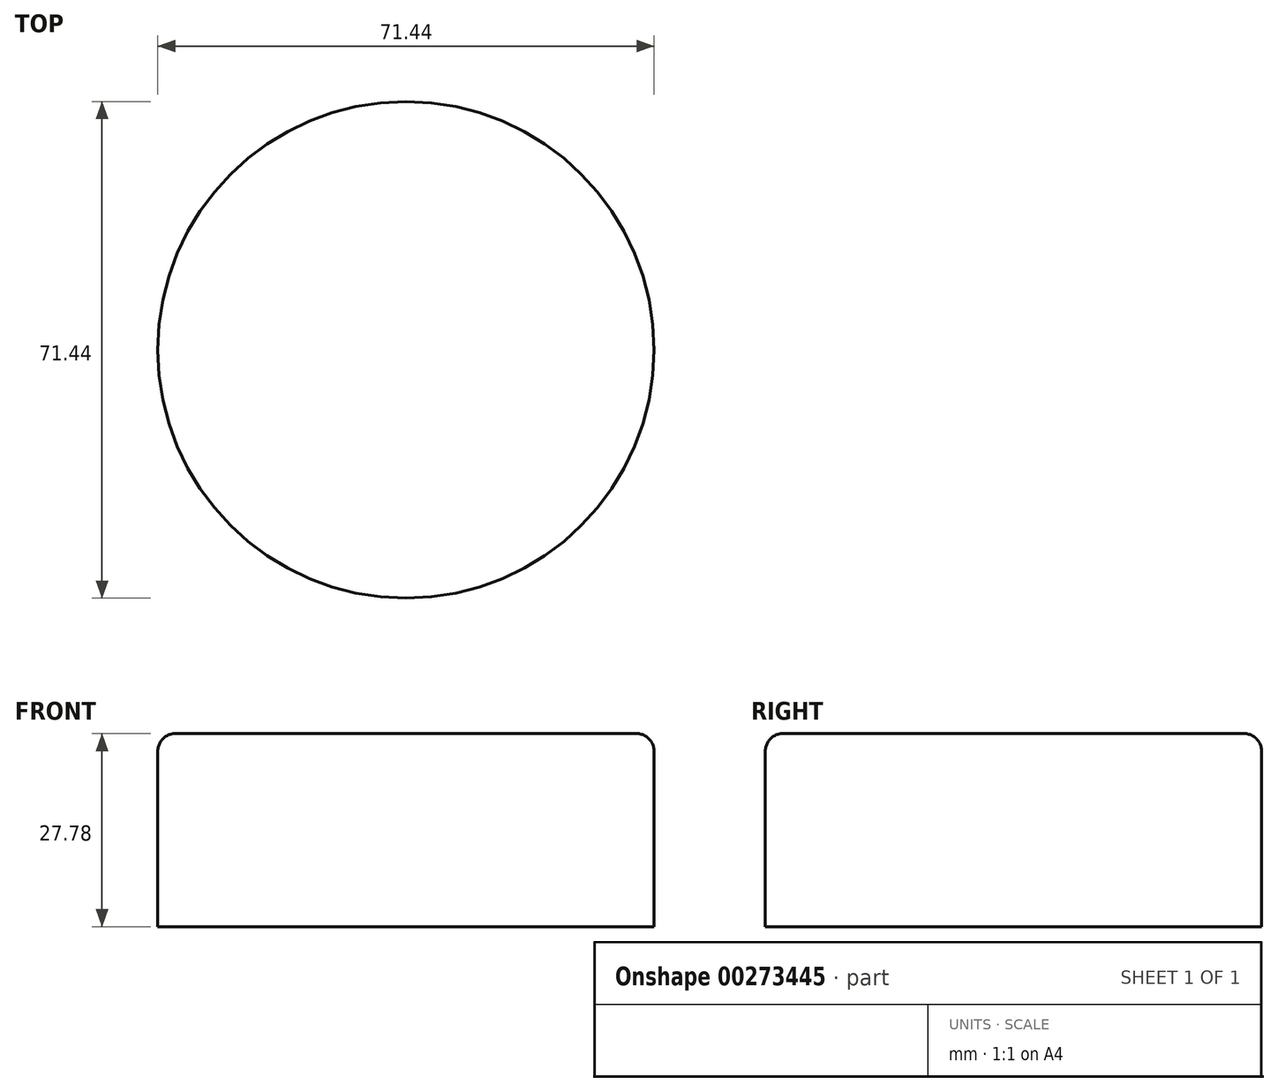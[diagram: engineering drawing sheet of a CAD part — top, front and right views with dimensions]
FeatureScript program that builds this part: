
annotation { "Feature Type Name" : "Feature", "Feature Type Description" : "" }
export const myFeature = defineFeature(function(context is Context, id is Id, definition is map)
    precondition{}
    {
        {
            var Q0;
            Q0=qCreatedBy(makeId("Top.planeOp"),FACE);
            var sketch = newSketch(context, id + "F0", { "sketchPlane" : qUnion([Q0])});
            skCircle(sketch, "E0", {"center": v(0, 0) * mm, "radius": 35.72 * mm});
            skSolve(sketch);
        }
        {
            var Q0;
            Q0=makeQuery(id+"F0.imprint","IMPRINT",FACE,{"disambiguationData":[TD([[makeQuery(id+"F0.imprint","IMPRINT",EDGE,{"derivedFrom":sQuery(id+"F0.wireOp",EDGE,"E0")}),1.0]])]});
            var Q1;
            Q1=sQuery(id+"F0.wireOp",EDGE,"E0");
            extrude(context, id + "F1", {"entities" : qUnion([Q0]), "surfaceEntities" : qUnion([Q1]), "depth" : 27.78 * mm});
        }
        {
            var Q0;
            Q0=makeQuery(id+"F1.opExtrude","CAP_EDGE",EDGE,{"disambiguationData":[OSD([sQuery(id+"F0.wireOp",EDGE,"E0")])],"isStart":false});
            fillet(context, id + "F2", {"entities" : qUnion([Q0]), "radius" : 2.54 * mm, "tangentPropagation" : true, "allowEdgeOverflow" : false});
        }
    });
